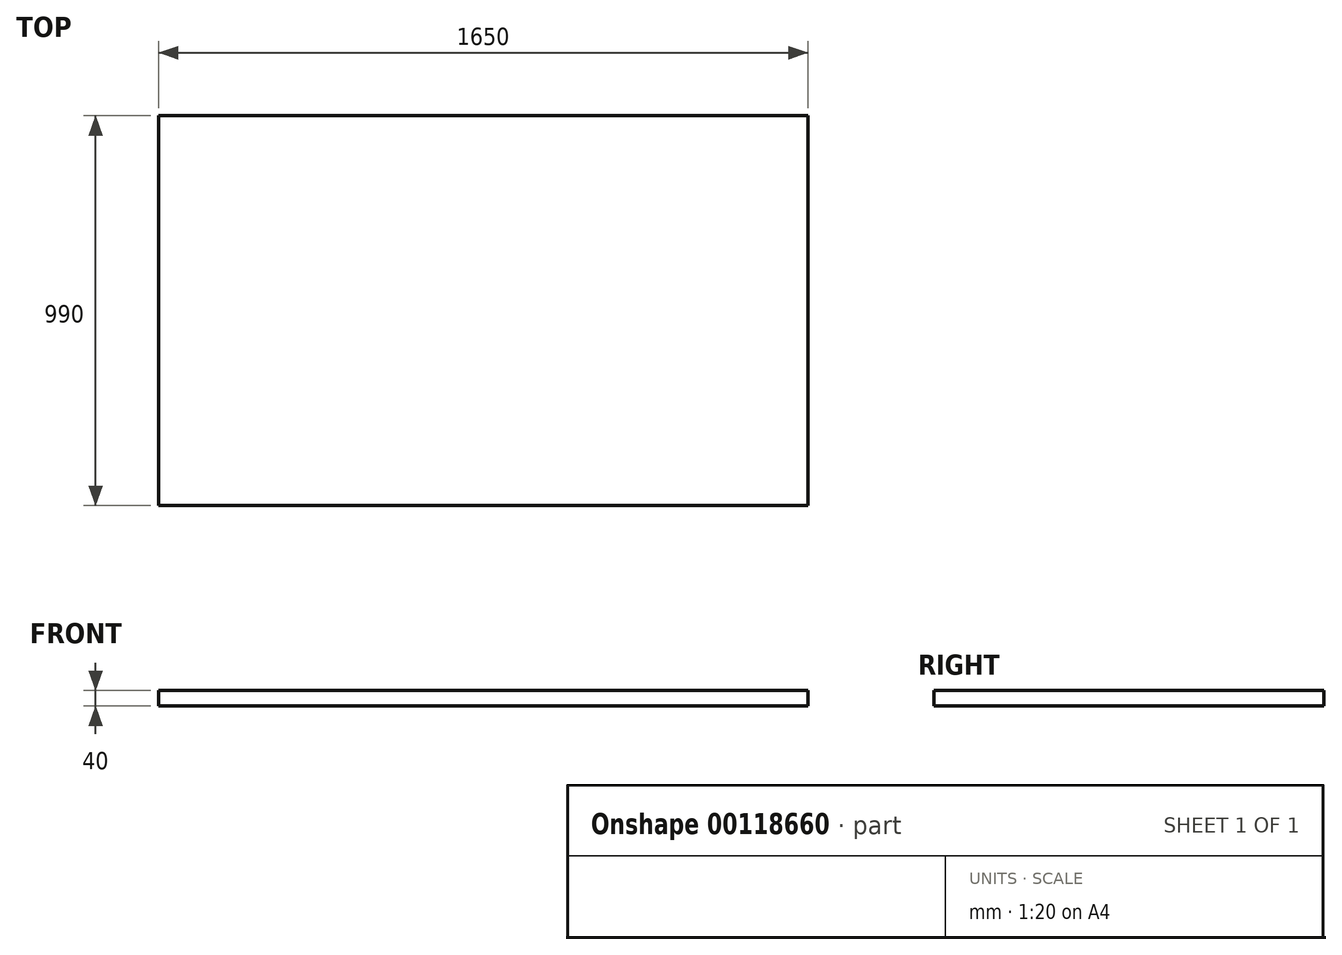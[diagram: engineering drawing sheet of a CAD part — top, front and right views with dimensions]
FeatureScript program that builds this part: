
annotation { "Feature Type Name" : "Feature", "Feature Type Description" : "" }
export const myFeature = defineFeature(function(context is Context, id is Id, definition is map)
    precondition{}
    {
        {
            var Q0;
            Q0=qCreatedBy(makeId("Top.planeOp"),FACE);
            var sketch = newSketch(context, id + "F0", { "sketchPlane" : qUnion([Q0])});
            skLineSegment(sketch, "E0.bottom", {"start": v(0, 0) * mm, "end": v(1650, 0) * mm});
            skLineSegment(sketch, "E0.top", {"start": v(0, 990) * mm, "end": v(1650, 990) * mm});
            skLineSegment(sketch, "E0.left", {"start": v(0, 0) * mm, "end": v(0, 990) * mm});
            skLineSegment(sketch, "E0.right", {"start": v(1650, 0) * mm, "end": v(1650, 990) * mm});
            skSolve(sketch);
        }
        {
            var Q0;
            Q0=makeQuery(id+"F0.imprint","IMPRINT",FACE,{"disambiguationData":[TD([[makeQuery(id+"F0.imprint","IMPRINT",EDGE,{"derivedFrom":sQuery(id+"F0.wireOp",EDGE,"E0.bottom")}),1.0]])]});
            extrude(context, id + "F1", {"entities" : qUnion([Q0]), "depth" : 40 * mm});
        }
    });
